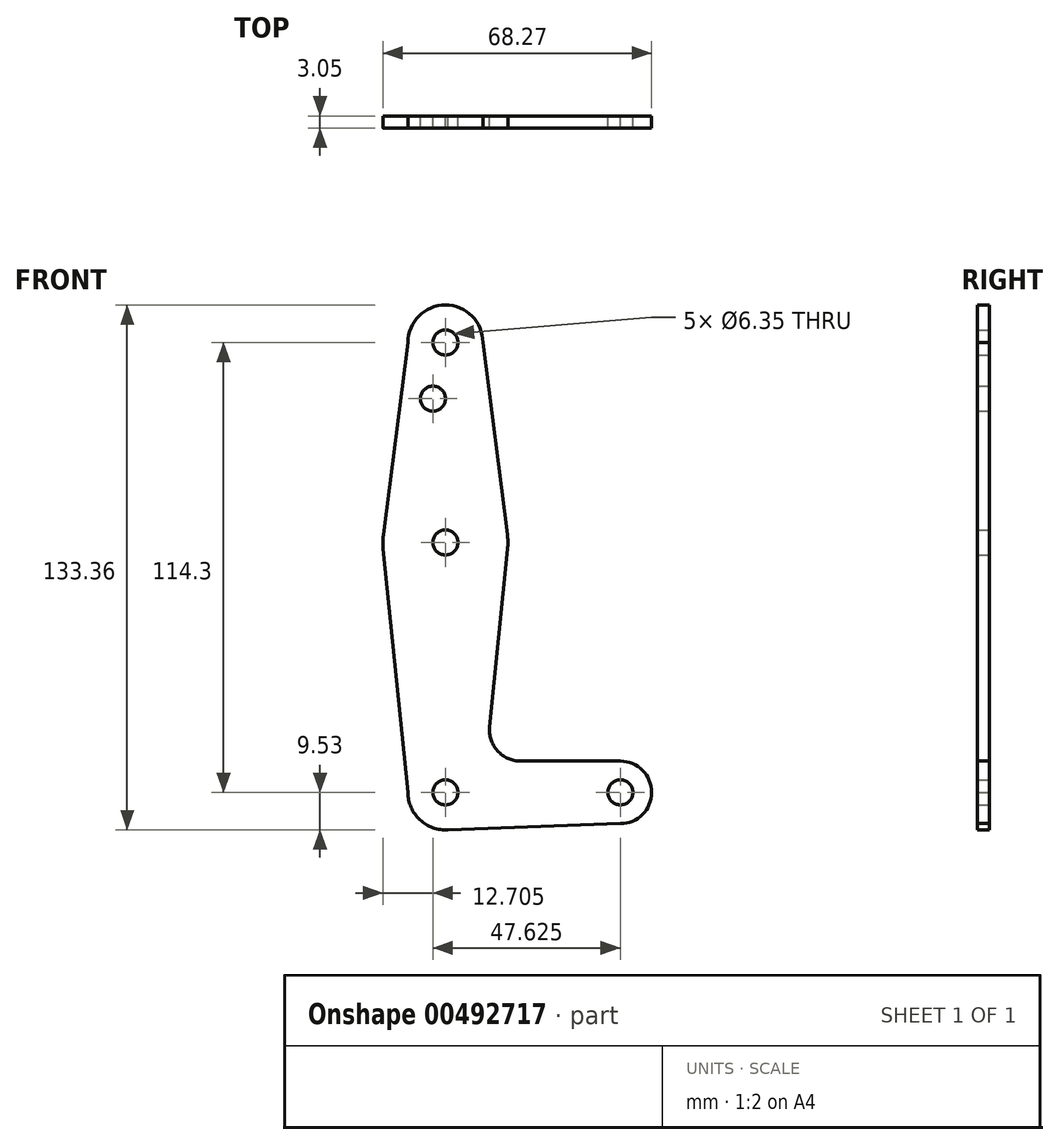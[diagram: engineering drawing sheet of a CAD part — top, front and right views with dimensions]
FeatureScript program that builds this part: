
annotation { "Feature Type Name" : "Feature", "Feature Type Description" : "" }
export const myFeature = defineFeature(function(context is Context, id is Id, definition is map)
    precondition{}
    {
        {
            var Q0;
            Q0=qCreatedBy(makeId("Front.planeOp"),FACE);
            var sketch = newSketch(context, id + "F0", { "sketchPlane" : qUnion([Q0])});
            skLineSegment(sketch, "E0", {"start": v(0, 0) * mm, "end": v(0, 63.5) * mm});
            skLineSegment(sketch, "E1", {"start": v(0, 63.5) * mm, "end": v(0, 114.3) * mm});
            skLineSegment(sketch, "E2", {"start": v(0, 0) * mm, "end": v(44.45, 0) * mm});
            skCircle(sketch, "E3", {"center": v(0, 0) * mm, "radius": 9.53 * mm});
            skCircle(sketch, "E4", {"center": v(44.45, 0) * mm, "radius": 7.94 * mm});
            skCircle(sketch, "E5", {"center": v(0, 63.5) * mm, "radius": 15.88 * mm});
            skCircle(sketch, "E6", {"center": v(0, 114.3) * mm, "radius": 9.53 * mm});
            skLineSegment(sketch, "E7", {"start": v(11.22, 16.69) * mm, "end": v(15.8, 61.9) * mm});
            skLineSegment(sketch, "E8", {"start": v(-9.53, 114.3) * mm, "end": v(-15.75, 65.5) * mm});
            skLineSegment(sketch, "E9", {"start": v(9.53, 114.3) * mm, "end": v(15.75, 65.5) * mm});
            skLineSegment(sketch, "E10", {"start": v(-9.52, 0) * mm, "end": v(-15.8, 61.9) * mm});
            skLineSegment(sketch, "E11", {"start": v(19.12, 7.94) * mm, "end": v(44.45, 7.94) * mm});
            skLineSegment(sketch, "E12", {"start": v(0, -9.53) * mm, "end": v(44.45, -7.94) * mm});
            skCircle(sketch, "E13", {"center": v(0, 114.3) * mm, "radius": 3.18 * mm});
            skCircle(sketch, "E14", {"center": v(0, 63.5) * mm, "radius": 3.18 * mm});
            skCircle(sketch, "E15", {"center": v(0, 0) * mm, "radius": 3.18 * mm});
            skCircle(sketch, "E16", {"center": v(44.45, 0) * mm, "radius": 3.18 * mm});
            skCircle(sketch, "E17", {"center": v(-3.18, 100.03) * mm, "radius": 3.18 * mm});
            skArc(sketch, "E18.filletArc", {"start": v(11.22, 16.69) * mm, "mid": v(13.23, 10.56) * mm, "end": v(19.12, 7.94) * mm});
            skSolve(sketch);
        }
        {
            var Q0;
            Q0 = qSketchRegion(id + "F0", true);
            var Q1;
            {var subQ0=sQuery(id+"F0.wireOp",EDGE,"E15");var subQ1=sQuery(id+"F0.wireOp",EDGE,"E0");var subQ2=makeQuery(id+"F0.imprint","INTERSECT",VERTEX,{"derivedFrom":[subQ1,subQ0]});Q1=makeQuery(id+"F0.imprint","IMPRINT",FACE,{"disambiguationData":[TD([[makeQuery(id+"F0.imprint","IMPRINT",EDGE,{"disambiguationData":[TD([[subQ2,-1.0]])],"derivedFrom":subQ1}),-1.0]])]});}
            extrude(context, id + "F1", {"entities" : qUnion([Q0, Q1]), "depth" : 3.05 * mm});
        }
    });
